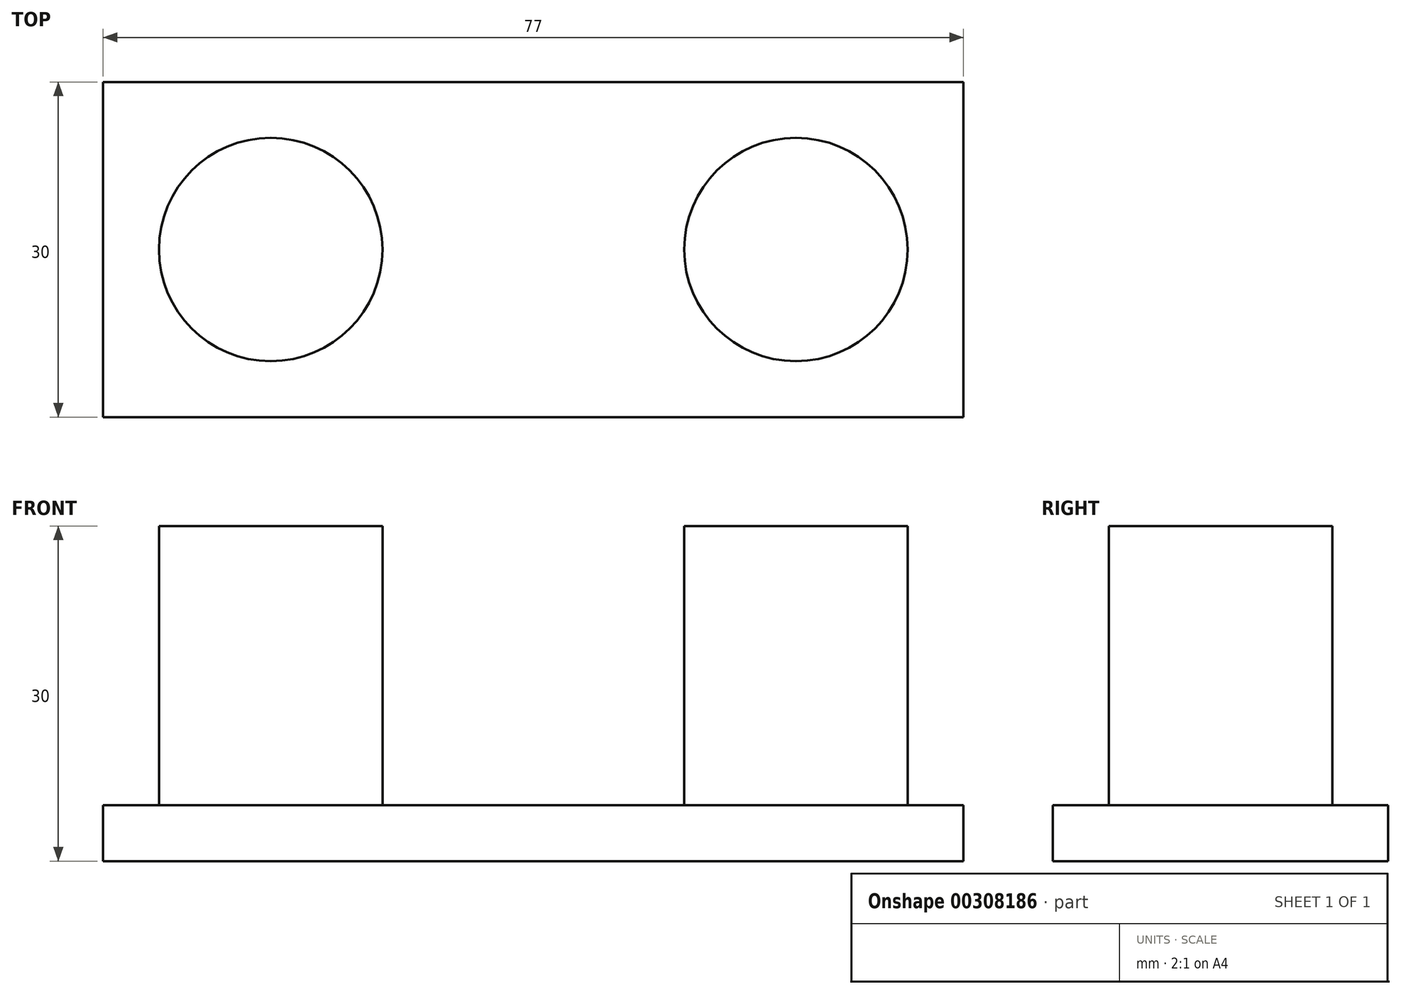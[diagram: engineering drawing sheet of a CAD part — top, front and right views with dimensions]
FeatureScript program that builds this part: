
annotation { "Feature Type Name" : "Feature", "Feature Type Description" : "" }
export const myFeature = defineFeature(function(context is Context, id is Id, definition is map)
    precondition{}
    {
        {
            var Q0;
            Q0=qCreatedBy(makeId("Top.planeOp"),FACE);
            var sketch = newSketch(context, id + "F0", { "sketchPlane" : qUnion([Q0])});
            skCircle(sketch, "E0", {"center": v(0, 0) * mm, "radius": 10 * mm});
            skLineSegment(sketch, "E1", {"start": v(0, 0) * mm, "end": v(47, 0) * mm});
            skCircle(sketch, "E2", {"center": v(47, 0) * mm, "radius": 10 * mm});
            skLineSegment(sketch, "E3", {"start": v(0, 0) * mm, "end": v(-15, 0) * mm});
            skLineSegment(sketch, "E4", {"start": v(-15, 0) * mm, "end": v(-15, -15) * mm});
            skLineSegment(sketch, "E5", {"start": v(-15, -15) * mm, "end": v(62, -15) * mm});
            skLineSegment(sketch, "E6", {"start": v(62, -15) * mm, "end": v(62, 0) * mm});
            skLineSegment(sketch, "E7", {"start": v(62, 0) * mm, "end": v(47, 0) * mm});
            skLineSegment(sketch, "E8", {"start": v(62, 15) * mm, "end": v(62, 0) * mm});
            skLineSegment(sketch, "E9", {"start": v(-15, 0) * mm, "end": v(-15, 15) * mm});
            skLineSegment(sketch, "E10", {"start": v(-15, 15) * mm, "end": v(62, 15) * mm});
            skSolve(sketch);
        }
        {
            var Q0;
            {var subQ0=sQuery(id+"F0.wireOp",EDGE,"E4");Q0=makeQuery(id+"F0.imprint","IMPRINT",FACE,{"disambiguationData":[TD([[makeQuery(id+"F0.imprint","IMPRINT",EDGE,{"derivedFrom":subQ0}),1.0]])]});}
            var sketch = newSketch(context, id + "F1", { "sketchPlane" : qUnion([Q0])});
            skSolve(sketch);
        }
        {
            var Q0;
            Q0=qSketchRegion(id+"F1",true);
            var Q1;
            {var subQ8=sQuery(id+"F0.wireOp",EDGE,"E8");Q1=makeQuery(id+"F0.imprint","IMPRINT",FACE,{"disambiguationData":[TD([[makeQuery(id+"F0.imprint","IMPRINT",EDGE,{"derivedFrom":subQ8}),-1.0]])]});}
            var Q2;
            {var subQ0=sQuery(id+"F0.wireOp",EDGE,"E4");Q2=makeQuery(id+"F0.imprint","IMPRINT",FACE,{"disambiguationData":[TD([[makeQuery(id+"F0.imprint","IMPRINT",EDGE,{"derivedFrom":subQ0}),1.0]])]});}
            extrude(context, id + "F2", {"entities" : qUnion([Q0, Q1, Q2]), "depth" : 5 * mm});
        }
        {
            var Q0;
            {var subQ0=sQuery(id+"F0.wireOp",EDGE,"E1");var subQ1=sQuery(id+"F0.wireOp",EDGE,"E0");var subQ2=makeQuery(id+"F0.imprint","INTERSECT",VERTEX,{"derivedFrom":[subQ1,subQ0]});Q0=makeQuery(id+"F0.imprint","IMPRINT",FACE,{"disambiguationData":[TD([[makeQuery(id+"F0.imprint","IMPRINT",EDGE,{"disambiguationData":[TD([[subQ2,-1.0]])],"derivedFrom":subQ1}),1.0]])]});}
            var Q1;
            {var subQ0=sQuery(id+"F0.wireOp",EDGE,"E1");var subQ1=sQuery(id+"F0.wireOp",EDGE,"E0");var subQ2=makeQuery(id+"F0.imprint","INTERSECT",VERTEX,{"derivedFrom":[subQ1,subQ0]});Q1=makeQuery(id+"F0.imprint","IMPRINT",FACE,{"disambiguationData":[TD([[makeQuery(id+"F0.imprint","IMPRINT",EDGE,{"disambiguationData":[TD([[subQ2,1.0]])],"derivedFrom":subQ1}),1.0]])]});}
            var Q2;
            {var subQ0=sQuery(id+"F0.wireOp",EDGE,"E7");var subQ1=sQuery(id+"F0.wireOp",EDGE,"E1");var subQ2=makeQuery(id+"F0.imprint","INTERSECT",VERTEX,{"derivedFrom":[subQ1,subQ0]});Q2=makeQuery(id+"F0.imprint","IMPRINT",FACE,{"disambiguationData":[TD([[makeQuery(id+"F0.imprint","IMPRINT",EDGE,{"disambiguationData":[TD([[subQ2,1.0]])],"derivedFrom":subQ1}),-1.0]])]});}
            var Q3;
            {var subQ0=sQuery(id+"F0.wireOp",EDGE,"E7");var subQ1=sQuery(id+"F0.wireOp",EDGE,"E1");var subQ2=makeQuery(id+"F0.imprint","INTERSECT",VERTEX,{"derivedFrom":[subQ1,subQ0]});Q3=makeQuery(id+"F0.imprint","IMPRINT",FACE,{"disambiguationData":[TD([[makeQuery(id+"F0.imprint","IMPRINT",EDGE,{"disambiguationData":[TD([[subQ2,1.0]])],"derivedFrom":subQ1}),1.0]])]});}
            extrude(context, id + "F3", {"entities" : qUnion([Q0, Q1, Q2, Q3]), "operationType" : NewBodyOperationType.ADD, "depth" : 30 * mm});
        }
    });
